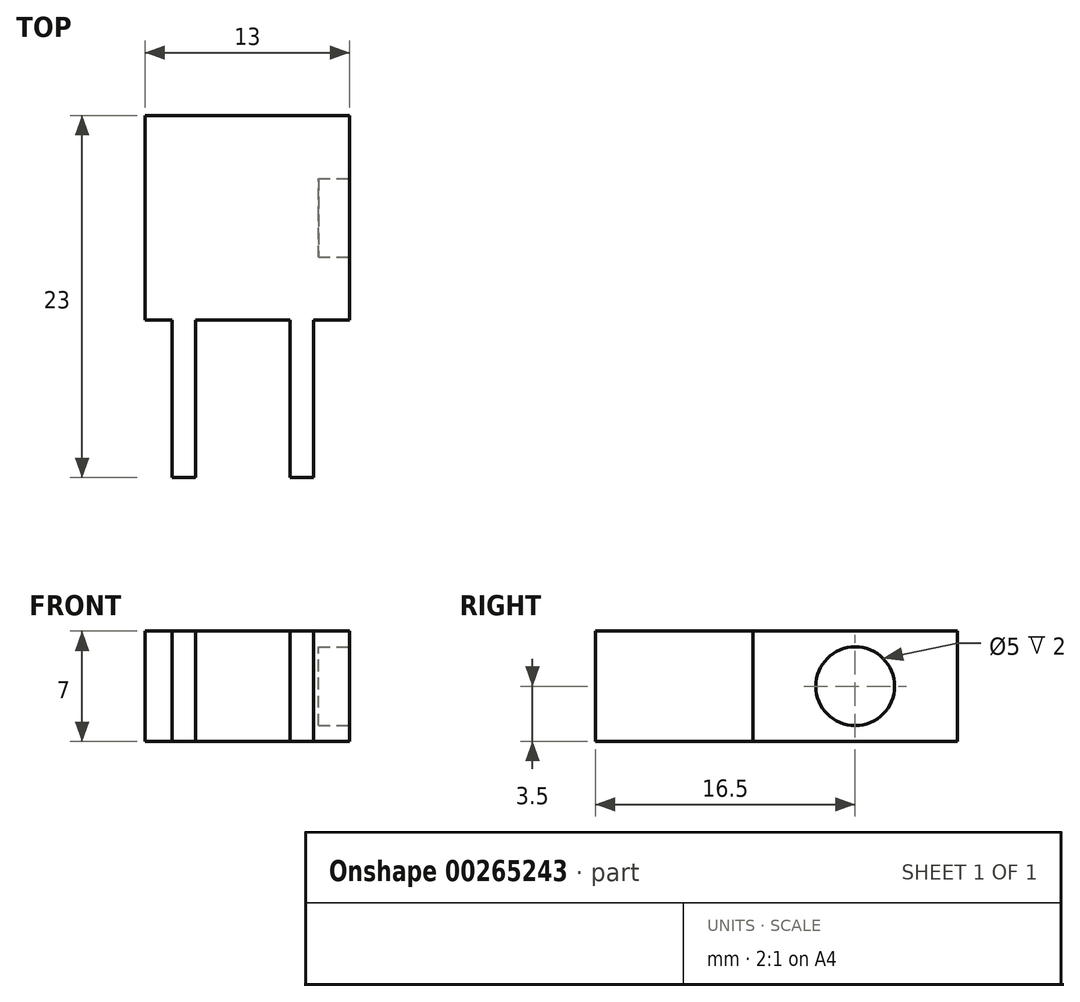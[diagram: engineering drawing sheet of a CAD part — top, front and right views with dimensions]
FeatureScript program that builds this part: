
annotation { "Feature Type Name" : "Feature", "Feature Type Description" : "" }
export const myFeature = defineFeature(function(context is Context, id is Id, definition is map)
    precondition{}
    {
        {
            var Q0;
            Q0=qCreatedBy(makeId("Top.planeOp"),FACE);
            var sketch = newSketch(context, id + "F0", { "sketchPlane" : qUnion([Q0])});
            skLineSegment(sketch, "E0.bottom", {"start": v(0, 0) * mm, "end": v(13, 0) * mm});
            skLineSegment(sketch, "E0.top", {"start": v(0, -13) * mm, "end": v(13, -13) * mm});
            skLineSegment(sketch, "E0.left", {"start": v(0, 0) * mm, "end": v(0, -13) * mm});
            skLineSegment(sketch, "E0.right", {"start": v(13, 0) * mm, "end": v(13, -13) * mm});
            skLineSegment(sketch, "E1", {"start": v(1.7, -13) * mm, "end": v(1.7, -23) * mm});
            skLineSegment(sketch, "E2", {"start": v(1.7, -23) * mm, "end": v(3.2, -23) * mm});
            skLineSegment(sketch, "E3", {"start": v(3.2, -23) * mm, "end": v(3.2, -13) * mm});
            skLineSegment(sketch, "E4", {"start": v(3.2, -13) * mm, "end": v(9.2, -13) * mm});
            skLineSegment(sketch, "E5", {"start": v(9.2, -13) * mm, "end": v(9.2, -23) * mm});
            skLineSegment(sketch, "E6", {"start": v(9.2, -23) * mm, "end": v(10.7, -23) * mm});
            skLineSegment(sketch, "E7", {"start": v(10.7, -23) * mm, "end": v(10.7, -13) * mm});
            skSolve(sketch);
        }
        {
            var Q0;
            Q0 = qSketchRegion(id + "F0", true);
            extrude(context, id + "F1", {"entities" : qUnion([Q0]), "depth" : 7 * mm});
        }
        {
            var Q0;
            Q0=makeQuery(id+"F1.opExtrude","SWEPT_FACE",FACE,{"disambiguationData":[OSD([sQuery(id+"F0.wireOp",EDGE,"E0.right")])]});
            var sketch = newSketch(context, id + "F2", { "sketchPlane" : qUnion([Q0])});
            skCircle(sketch, "E8", {"center": v(-6.5, 3.5) * mm, "radius": 2.5 * mm});
            skSolve(sketch);
        }
        {
            var Q0;
            Q0 = qSketchRegion(id + "F2", true);
            extrude(context, id + "F3", {"entities" : qUnion([Q0]), "operationType" : NewBodyOperationType.REMOVE, "oppositeDirection" : true, "depth" : 2 * mm});
        }
    });
